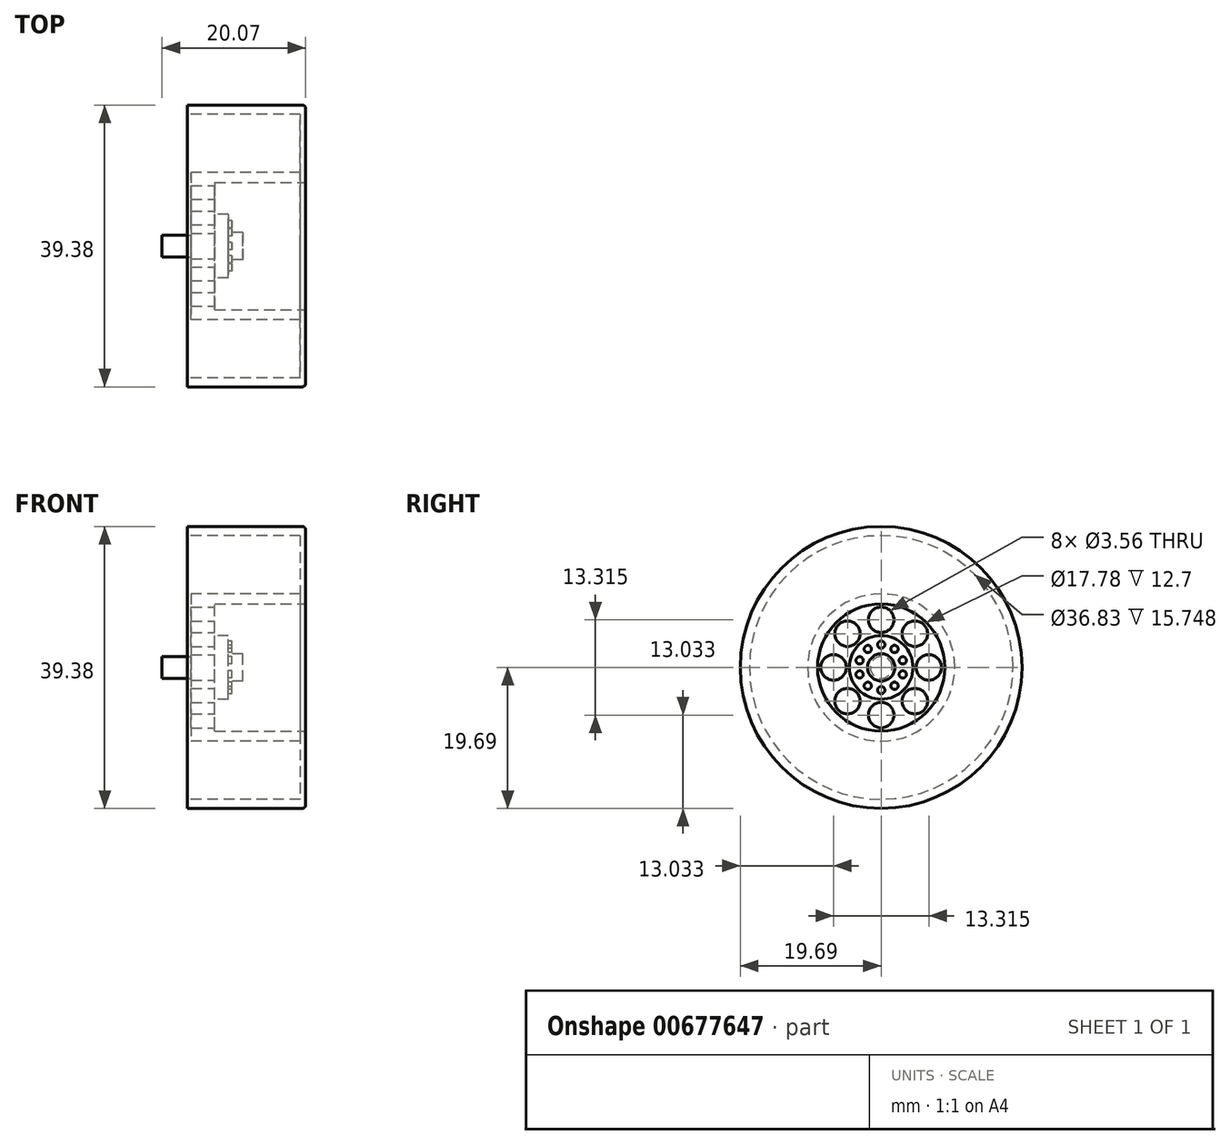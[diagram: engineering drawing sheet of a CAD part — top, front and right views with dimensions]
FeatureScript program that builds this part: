
annotation { "Feature Type Name" : "Feature", "Feature Type Description" : "" }
export const myFeature = defineFeature(function(context is Context, id is Id, definition is map)
    precondition{}
    {
        {
            var Q0;
            Q0=qCreatedBy(makeId("Right.planeOp"),FACE);
            var sketch = newSketch(context, id + "F0", { "sketchPlane" : qUnion([Q0])});
            skCircle(sketch, "E0", {"center": v(0, 0) * mm, "radius": 19.69 * mm});
            skSolve(sketch);
        }
        {
            var Q0;
            Q0=makeQuery(id+"F0.imprint","IMPRINT",FACE,{"disambiguationData":[TD([[makeQuery(id+"F0.imprint","IMPRINT",EDGE,{"derivedFrom":sQuery(id+"F0.wireOp",EDGE,"E0")}),1.0]])]});
            extrude(context, id + "F1", {"entities" : qUnion([Q0]), "depth" : 16.5 * mm, "offsetDistance" : 25.4 * mm});
        }
        {
            var Q0;
            Q0=makeQuery(id+"F1.opExtrude","CAP_FACE",FACE,{"disambiguationData":[OSD([sQuery(id+"F0.wireOp",EDGE,"E0")])],"isStart":false});
            var sketch = newSketch(context, id + "F2", { "sketchPlane" : qUnion([Q0])});
            skCircle(sketch, "E1", {"center": v(0, 0) * mm, "radius": 8.9 * mm});
            skSolve(sketch);
        }
        {
            var Q0;
            Q0=makeQuery(id+"F2.imprint","IMPRINT",FACE,{"disambiguationData":[TD([[makeQuery(id+"F2.imprint","IMPRINT",EDGE,{"derivedFrom":sQuery(id+"F2.wireOp",EDGE,"E1")}),1.0]])]});
            extrude(context, id + "F3", {"entities" : qUnion([Q0]), "operationType" : NewBodyOperationType.REMOVE, "oppositeDirection" : true, "depth" : 12.7 * mm, "offsetDistance" : 25.4 * mm});
        }
        {
            var Q0;
            Q0=makeQuery(id+"F3.boolean.opBoolean","COPY",FACE,{"derivedFrom":makeQuery(id+"F3.opExtrude","CAP_FACE",FACE,{"disambiguationData":[OSD([sQuery(id+"F2.wireOp",EDGE,"E1")])],"isStart":false})});
            var sketch = newSketch(context, id + "F4", { "sketchPlane" : qUnion([Q0])});
            skCircle(sketch, "E2", {"center": v(0, 0) * mm, "radius": 4.45 * mm});
            skSolve(sketch);
        }
        {
            var Q0;
            Q0=makeQuery(id+"F4.imprint","IMPRINT",FACE,{"disambiguationData":[TD([[makeQuery(id+"F4.imprint","IMPRINT",EDGE,{"derivedFrom":sQuery(id+"F4.wireOp",EDGE,"E2")}),1.0]])]});
            extrude(context, id + "F5", {"entities" : qUnion([Q0]), "operationType" : NewBodyOperationType.ADD, "depth" : 1.9 * mm, "offsetDistance" : 25.4 * mm});
        }
        {
            var Q0;
            Q0=makeQuery(id+"F5.opExtrude","CAP_FACE",FACE,{"disambiguationData":[OSD([sQuery(id+"F4.wireOp",EDGE,"E2")])],"isStart":false});
            var sketch = newSketch(context, id + "F6", { "sketchPlane" : qUnion([Q0])});
            skCircle(sketch, "E3", {"center": v(0, 0) * mm, "radius": 1.9 * mm});
            skSolve(sketch);
        }
        {
            var Q0;
            Q0=makeQuery(id+"F6.imprint","IMPRINT",FACE,{"disambiguationData":[TD([[makeQuery(id+"F6.imprint","IMPRINT",EDGE,{"derivedFrom":sQuery(id+"F6.wireOp",EDGE,"E3")}),1.0]])]});
            extrude(context, id + "F7", {"entities" : qUnion([Q0]), "operationType" : NewBodyOperationType.ADD, "depth" : 2.03 * mm, "offsetDistance" : 25.4 * mm});
        }
        {
            var Q0;
            Q0=makeQuery(id+"F3.boolean.opBoolean","COPY",FACE,{"derivedFrom":makeQuery(id+"F3.opExtrude","CAP_FACE",FACE,{"disambiguationData":[OSD([sQuery(id+"F2.wireOp",EDGE,"E1")])],"isStart":false})});
            var sketch = newSketch(context, id + "F8", { "sketchPlane" : qUnion([Q0])});
            skCircle(sketch, "E4", {"center": v(0, 6.66) * mm, "radius": 1.78 * mm});
            skCircle(sketch, "E5.1.0", {"center": v(-4.7, 4.7) * mm, "radius": 1.78 * mm});
            skCircle(sketch, "E5.2.0", {"center": v(-6.66, 0) * mm, "radius": 1.78 * mm});
            skCircle(sketch, "E5.3.0", {"center": v(-4.7, -4.7) * mm, "radius": 1.78 * mm});
            skCircle(sketch, "E5.4.0", {"center": v(0, -6.66) * mm, "radius": 1.78 * mm});
            skCircle(sketch, "E5.5.0", {"center": v(4.7, -4.7) * mm, "radius": 1.78 * mm});
            skCircle(sketch, "E5.6.0", {"center": v(6.66, 0) * mm, "radius": 1.78 * mm});
            skCircle(sketch, "E5.7.0", {"center": v(4.7, 4.7) * mm, "radius": 1.78 * mm});
            skPoint(sketch, "E5.center", {"position": v(0, 0) * mm});
            skSolve(sketch);
        }
        {
            var Q0;
            Q0 = qSketchRegion(id + "F8", true);
            extrude(context, id + "F9", {"entities" : qUnion([Q0]), "operationType" : NewBodyOperationType.REMOVE, "oppositeDirection" : true, "depth" : 5.08 * mm, "offsetDistance" : 25.4 * mm});
        }
        {
            var Q0;
            Q0=makeQuery(id+"F5.opExtrude","CAP_FACE",FACE,{"disambiguationData":[OSD([sQuery(id+"F4.wireOp",EDGE,"E2")])],"isStart":false});
            var sketch = newSketch(context, id + "F10", { "sketchPlane" : qUnion([Q0])});
            skCircle(sketch, "E6", {"center": v(0, 3.17) * mm, "radius": 0.5 * mm});
            skCircle(sketch, "E7.1.0", {"center": v(-1.87, 2.57) * mm, "radius": 0.5 * mm});
            skCircle(sketch, "E7.2.0", {"center": v(-3.02, 0.98) * mm, "radius": 0.5 * mm});
            skCircle(sketch, "E7.3.0", {"center": v(-3.02, -0.98) * mm, "radius": 0.5 * mm});
            skCircle(sketch, "E7.4.0", {"center": v(-1.87, -2.57) * mm, "radius": 0.5 * mm});
            skCircle(sketch, "E7.5.0", {"center": v(0, -3.17) * mm, "radius": 0.5 * mm});
            skCircle(sketch, "E7.6.0", {"center": v(1.87, -2.57) * mm, "radius": 0.5 * mm});
            skCircle(sketch, "E7.7.0", {"center": v(3.02, -0.98) * mm, "radius": 0.5 * mm});
            skCircle(sketch, "E7.8.0", {"center": v(3.02, 0.98) * mm, "radius": 0.5 * mm});
            skCircle(sketch, "E7.9.0", {"center": v(1.87, 2.57) * mm, "radius": 0.5 * mm});
            skPoint(sketch, "E7.center", {"position": v(0, 0) * mm});
            skSolve(sketch);
        }
        {
            var Q0;
            Q0 = qSketchRegion(id + "F10", true);
            extrude(context, id + "F11", {"entities" : qUnion([Q0]), "operationType" : NewBodyOperationType.ADD, "depth" : 0.5 * mm, "offsetDistance" : 25.4 * mm});
        }
        {
            var Q0;
            Q0=makeQuery(id+"F1.opExtrude","CAP_FACE",FACE,{"disambiguationData":[OSD([sQuery(id+"F0.wireOp",EDGE,"E0")])],"isStart":true});
            var sketch = newSketch(context, id + "F12", { "sketchPlane" : qUnion([Q0])});
            skCircle(sketch, "E8", {"center": v(0, 0) * mm, "radius": 1.52 * mm});
            skSolve(sketch);
        }
        {
            var Q0;
            Q0=makeQuery(id+"F12.imprint","IMPRINT",FACE,{"disambiguationData":[TD([[makeQuery(id+"F12.imprint","IMPRINT",EDGE,{"derivedFrom":sQuery(id+"F12.wireOp",EDGE,"E8")}),1.0]])]});
            extrude(context, id + "F13", {"entities" : qUnion([Q0]), "operationType" : NewBodyOperationType.ADD, "depth" : 3.56 * mm, "offsetDistance" : 25.4 * mm});
        }
        {
            var Q0;
            Q0=makeQuery(id+"F1.opExtrude","CAP_FACE",FACE,{"disambiguationData":[OSD([sQuery(id+"F0.wireOp",EDGE,"E0")])],"isStart":true});
            var sketch = newSketch(context, id + "F14", { "sketchPlane" : qUnion([Q0])});
            skCircle(sketch, "E9", {"center": v(0, 0) * mm, "radius": 10.29 * mm});
            skSolve(sketch);
        }
        {
            var Q0;
            Q0=makeQuery(id+"F14.imprint","IMPRINT",FACE,{"disambiguationData":[TD([[makeQuery(id+"F14.imprint","IMPRINT",EDGE,{"derivedFrom":sQuery(id+"F14.wireOp",EDGE,"E9")}),1.0]])]});
            extrude(context, id + "F15", {"entities" : qUnion([Q0]), "operationType" : NewBodyOperationType.REMOVE, "oppositeDirection" : true, "depth" : 0.5 * mm, "offsetDistance" : 25.4 * mm});
        }
        {
            var Q0;
            Q0=makeQuery(id+"F1.opExtrude","CAP_FACE",FACE,{"disambiguationData":[OSD([sQuery(id+"F0.wireOp",EDGE,"E0")])],"isStart":true});
            var sketch = newSketch(context, id + "F16", { "sketchPlane" : qUnion([Q0])});
            skCircle(sketch, "E10", {"center": v(0, 0) * mm, "radius": 18.41 * mm});
            skSolve(sketch);
        }
        {
            var Q0;
            Q0=makeQuery(id+"F16.imprint","IMPRINT",FACE,{"disambiguationData":[TD([[makeQuery(id+"F16.imprint","IMPRINT",EDGE,{"derivedFrom":sQuery(id+"F16.wireOp",EDGE,"E10")}),1.0]])]});
            extrude(context, id + "F17", {"entities" : qUnion([Q0]), "operationType" : NewBodyOperationType.REMOVE, "oppositeDirection" : true, "depth" : 15.75 * mm, "offsetDistance" : 25.4 * mm});
        }
        {
            var Q0;
            Q0=makeQuery(id+"F1.opExtrude","CAP_EDGE",EDGE,{"disambiguationData":[OSD([sQuery(id+"F0.wireOp",EDGE,"E0")])],"isStart":false});
            fillet(context, id + "F18", {"entities" : qUnion([Q0]), "radius" : 0.5 * mm, "tangentPropagation" : true, "allowEdgeOverflow" : false});
        }
    });
